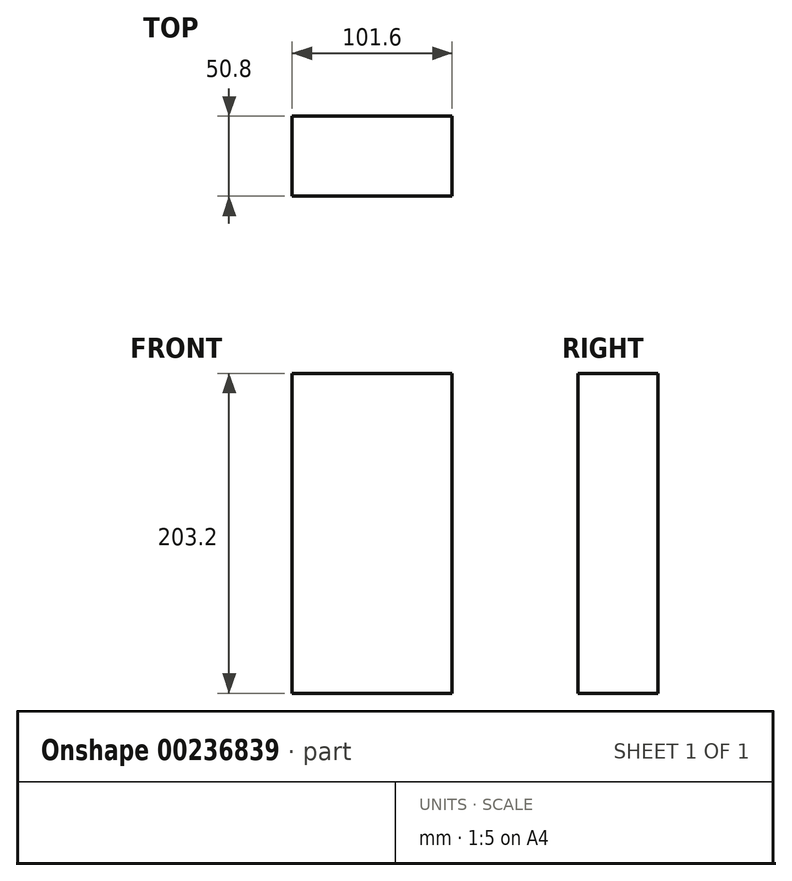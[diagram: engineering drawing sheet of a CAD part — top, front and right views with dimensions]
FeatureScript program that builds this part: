
annotation { "Feature Type Name" : "Feature", "Feature Type Description" : "" }
export const myFeature = defineFeature(function(context is Context, id is Id, definition is map)
    precondition{}
    {
        {
            var Q0;
            Q0=qCreatedBy(makeId("Front.planeOp"),FACE);
            var sketch = newSketch(context, id + "F0", { "sketchPlane" : qUnion([Q0])});
            skLineSegment(sketch, "E0.bottom", {"start": v(-50.8, 101.6) * mm, "end": v(50.8, 101.6) * mm});
            skLineSegment(sketch, "E0.top", {"start": v(-50.8, -101.6) * mm, "end": v(50.8, -101.6) * mm});
            skLineSegment(sketch, "E0.left", {"start": v(-50.8, 101.6) * mm, "end": v(-50.8, -101.6) * mm});
            skLineSegment(sketch, "E0.right", {"start": v(50.8, 101.6) * mm, "end": v(50.8, -101.6) * mm});
            skPoint(sketch, "E0.middle", {"position": v(0, 0) * mm});
            skSolve(sketch);
        }
        {
            var Q0;
            Q0=qSketchRegion(id+"F0",true);
            extrude(context, id + "F1", {"entities" : qUnion([Q0]), "endBound" : BoundingType.SYMMETRIC, "depth" : 50.8 * mm});
        }
    });
